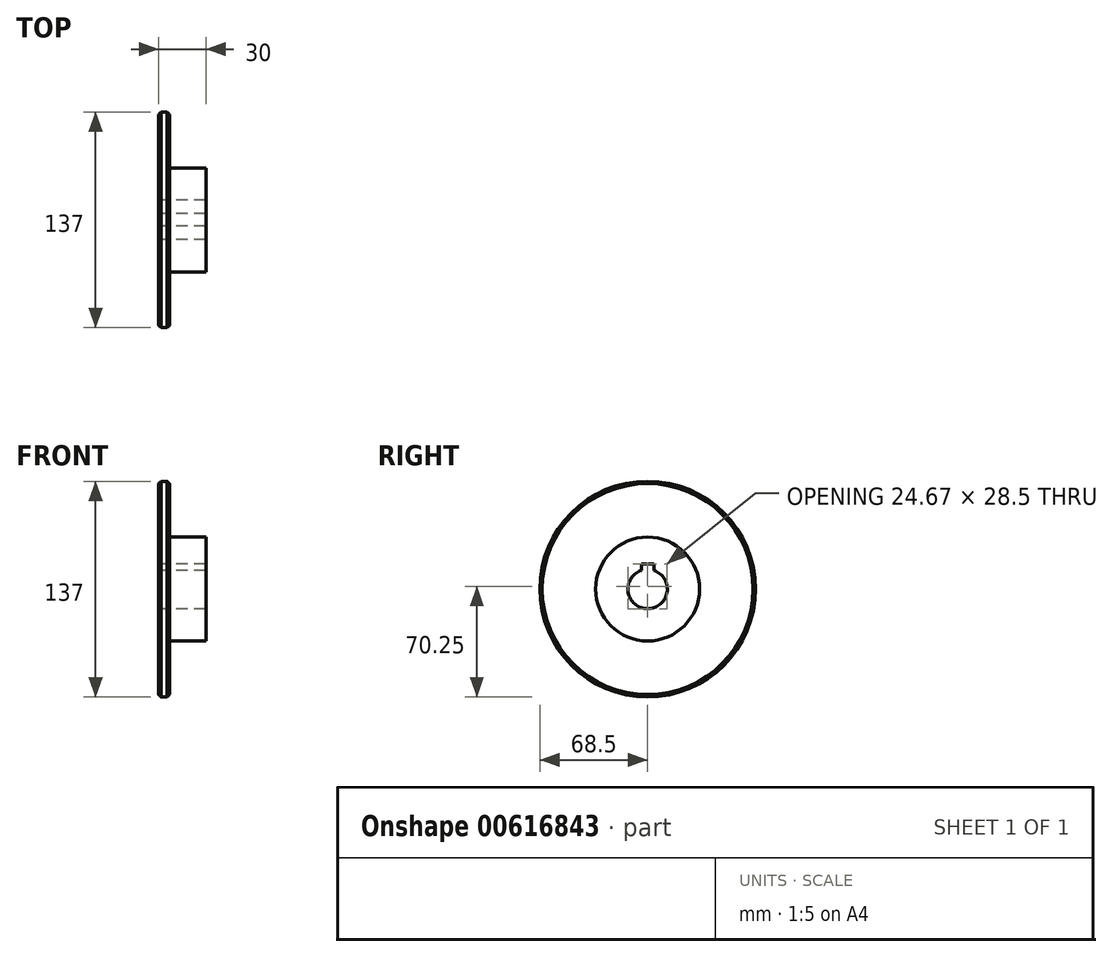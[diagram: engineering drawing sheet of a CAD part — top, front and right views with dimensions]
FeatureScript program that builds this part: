
annotation { "Feature Type Name" : "Feature", "Feature Type Description" : "" }
export const myFeature = defineFeature(function(context is Context, id is Id, definition is map)
    precondition{}
    {
        {
            var Q0;
            Q0=qCreatedBy(makeId("Front.planeOp"),FACE);
            var sketch = newSketch(context, id + "F0", { "sketchPlane" : qUnion([Q0])});
            skLineSegment(sketch, "E0", {"start": v(0, 68.5) * mm, "end": v(0, 12.5) * mm});
            skLineSegment(sketch, "E1", {"start": v(0, 12.5) * mm, "end": v(30, 12.5) * mm});
            skLineSegment(sketch, "E2", {"start": v(30, 12.5) * mm, "end": v(30, 33) * mm});
            skLineSegment(sketch, "E3", {"start": v(30, 33) * mm, "end": v(7, 33) * mm});
            skLineSegment(sketch, "E4", {"start": v(7, 33) * mm, "end": v(7, 68.5) * mm});
            skLineSegment(sketch, "E5", {"start": v(7, 68.5) * mm, "end": v(0, 68.5) * mm});
            skLineSegment(sketch, "E6", {"start": v(0, 0) * mm, "end": v(67.6, 0) * mm, "construction": true});
            skSolve(sketch);
        }
        {
            var Q0;
            Q0 = qSketchRegion(id + "F0", true);
            var Q1;
            Q1=sQuery(id+"F0.wireOp",EDGE,"E6");
            revolve(context, id + "F1", {"surfaceOperationType" : NewSurfaceOperationType.NEW, "entities" : qUnion([Q0]), "axis" : qUnion([Q1]), "revolveType" : RevolveType.FULL});
        }
        {
            var Q0;
            Q0=qCreatedBy(makeId("Right.planeOp"),FACE);
            var sketch = newSketch(context, id + "F2", { "sketchPlane" : qUnion([Q0])});
            skLineSegment(sketch, "E7.bottom", {"start": v(4, 6) * mm, "end": v(-4, 6) * mm});
            skLineSegment(sketch, "E7.top", {"start": v(4, 16) * mm, "end": v(-4, 16) * mm});
            skLineSegment(sketch, "E7.left", {"start": v(4, 6) * mm, "end": v(4, 16) * mm});
            skLineSegment(sketch, "E7.right", {"start": v(-4, 6) * mm, "end": v(-4, 16) * mm});
            skPoint(sketch, "E7.middle", {"position": v(0, 11) * mm});
            skCircle(sketch, "E8.0", {"center": v(0, 0) * mm, "radius": 12.5 * mm, "construction": true});
            skSolve(sketch);
        }
        {
            var Q0;
            Q0 = qSketchRegion(id + "F2", true);
            extrude(context, id + "F3", {"entities" : qUnion([Q0]), "operationType" : NewBodyOperationType.REMOVE, "endBound" : BoundingType.THROUGH_ALL, "depth" : 25 * mm, "offsetDistance" : 25 * mm});
        }
        {
            var Q0;
            Q0=makeQuery(id+"F1.opRevolve","SWEPT_EDGE",EDGE,{"disambiguationData":[OSD([sQuery(id+"F0.wireOp",EDGE,"E4"),sQuery(id+"F0.wireOp",EDGE,"E5")])]});
            var Q1;
            Q1=makeQuery(id+"F1.opRevolve","SWEPT_EDGE",EDGE,{"disambiguationData":[OSD([sQuery(id+"F0.wireOp",EDGE,"E0"),sQuery(id+"F0.wireOp",EDGE,"E5")])]});
            chamfer(context, id + "F4", {"entities" : qUnion([Q0, Q1]), "width" : 1.5 * mm, "tangentPropagation" : true});
        }
    });
